# Revit family: КРОН-50
name_source: partatom
category: Арматура трубопроводов
units: mm (PartAtom-declared; Revit-internal decimal feet)

## family parameters
Всегда вертикально = Да
На основе рабочей плоскости = Нет
Общий = Нет
При загрузке вырезать с полостями = Нет
Размер круглого соединителя = Использовать диаметр
Тип детали = Клапан - Вставляется

## types (6) — shared parameters
ADSK_Единица измерения = шт.
ADSK_Завод-изготовитель = РУП "БЕЛГАЗТЕХНИКА"
ADSK_Количество = 1
ADSK_Марка = КРОН-50
ADSK_Масса_Текст = 60,0 кг
zero-valued in all types: Отметка по умолчанию

## per-type parameters (varying)
| type | ADSK_Диапазон выходного давления, МПа | ADSK_Наименование | исполнение Л | исполнение П |
| исполнение Л 0,3-0,6 | 0,3-0,6 | Регулятор КРОН-50-Л-(0,3-0,6) ТУ BY 100270876.165-2012 | Да | Нет |
| исполнение Л 0,01-0,05 | 0,01-0,05 | Регулятор КРОН-50-Л-(0,01-0,05) ТУ BY 100270876.165-2012 | Да | Нет |
| исполнение П 0,01-0,05 | 0,01-0,05 | Регулятор КРОН-50-П-(0,01-0,05) ТУ BY 100270876.165-2012 | Нет | Да |
| исполнение Л 0,05-0,3 | 0,05-0,3 | Регулятор КРОН-50-Л-(0,05-0,3) ТУ BY 100270876.165-2012 | Да | Нет |
| исполнение П 0,05-0,3 | 0,05-0,3 | Регулятор КРОН-50-П-(0,05-0,3) ТУ BY 100270876.165-2012 | Нет | Да |
| исполнение П 0,3-0,6 | 0,3-0,6 | Регулятор КРОН-50-П-(0,3-0,6) ТУ BY 100270876.165-2012 | Нет | Да |
